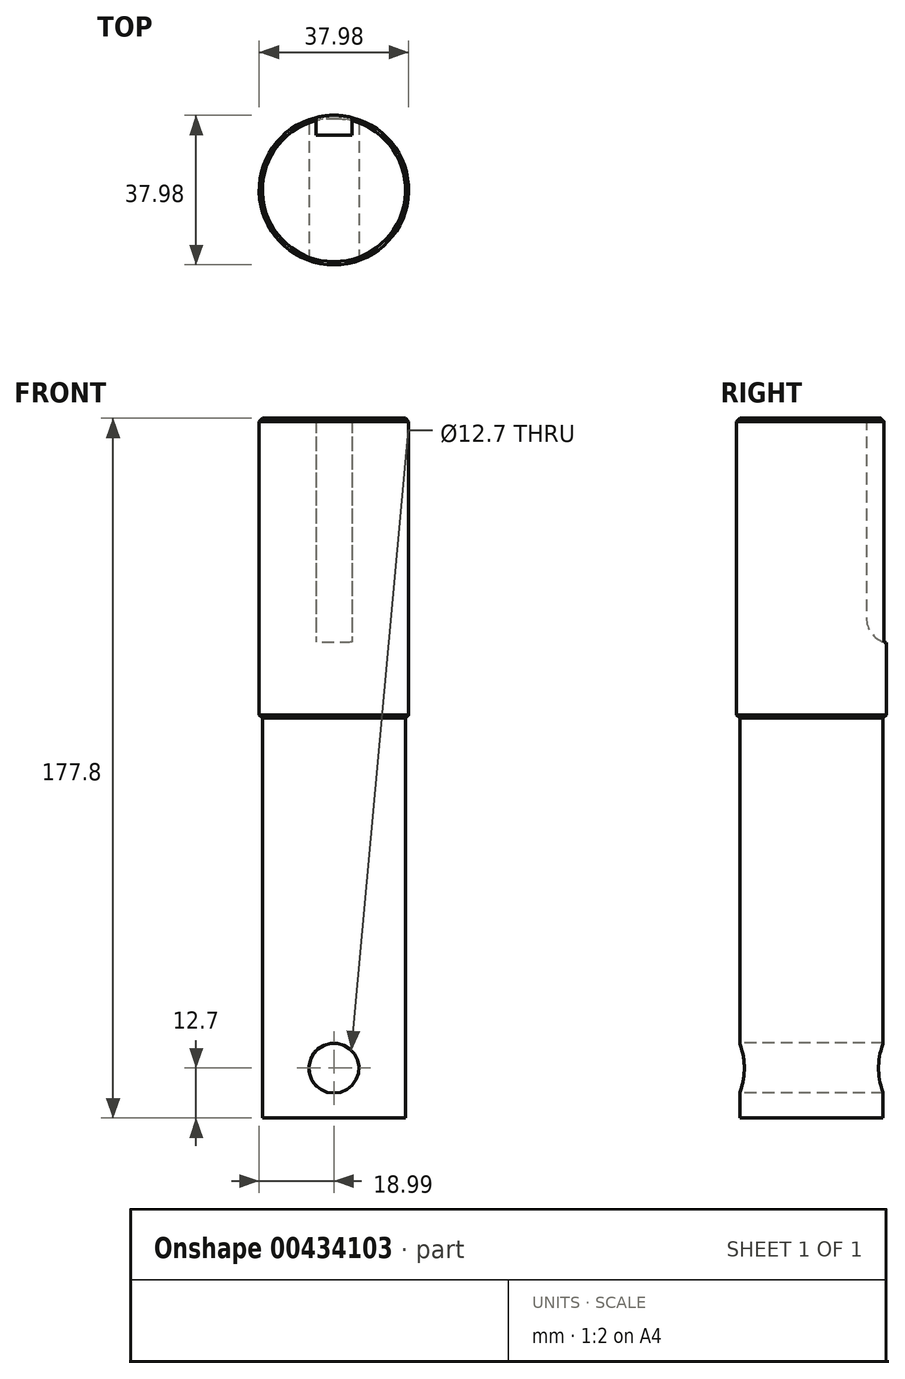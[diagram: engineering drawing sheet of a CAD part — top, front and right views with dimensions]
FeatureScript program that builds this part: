
annotation { "Feature Type Name" : "Feature", "Feature Type Description" : "" }
export const myFeature = defineFeature(function(context is Context, id is Id, definition is map)
    precondition{}
    {
        {
            var Q0;
            Q0=qCreatedBy(makeId("Top.planeOp"),FACE);
            var sketch = newSketch(context, id + "F0", { "sketchPlane" : qUnion([Q0])});
            skCircle(sketch, "E0", {"center": v(0, 0) * mm, "radius": 18.99 * mm});
            skSolve(sketch);
        }
        {
            var Q0;
            Q0=makeQuery(id+"F0.imprint","IMPRINT",FACE,{"disambiguationData":[TD([[makeQuery(id+"F0.imprint","IMPRINT",EDGE,{"derivedFrom":sQuery(id+"F0.wireOp",EDGE,"E0")}),1.0]])]});
            extrude(context, id + "F1", {"entities" : qUnion([Q0]), "endBound" : BoundingType.SYMMETRIC, "depth" : 76.2 * mm});
        }
        {
            var Q0;
            Q0=makeQuery(id+"F1.opExtrude","CAP_EDGE",EDGE,{"disambiguationData":[OSD([sQuery(id+"F0.wireOp",EDGE,"E0")])],"isStart":false});
            var Q1;
            Q1=makeQuery(id+"F1.opExtrude","CAP_EDGE",EDGE,{"disambiguationData":[OSD([sQuery(id+"F0.wireOp",EDGE,"E0")])],"isStart":true});
            chamfer(context, id + "F2", {"entities" : qUnion([Q0, Q1]), "width" : 0.8 * mm, "tangentPropagation" : true});
        }
        {
            var Q0;
            Q0=qCreatedBy(makeId("Right.planeOp"),FACE);
            var sketch = newSketch(context, id + "F3", { "sketchPlane" : qUnion([Q0])});
            skLineSegment(sketch, "E1", {"start": v(13.97, 38.1) * mm, "end": v(13.97, -12.7) * mm});
            skArc(sketch, "E2", {"start": v(13.97, -12.7) * mm, "mid": v(15.4, -16.72) * mm, "end": v(19.05, -18.92) * mm});
            skLineSegment(sketch, "E3", {"start": v(13.97, 38.1) * mm, "end": v(19.05, 38.1) * mm});
            skLineSegment(sketch, "E4", {"start": v(19.05, 38.1) * mm, "end": v(19.05, -18.92) * mm});
            skSolve(sketch);
        }
        {
            var Q0;
            Q0 = qSketchRegion(id + "F3", true);
            extrude(context, id + "F4", {"entities" : qUnion([Q0]), "operationType" : NewBodyOperationType.REMOVE, "endBound" : BoundingType.SYMMETRIC, "depth" : 9.14 * mm});
        }
        {
            var Q0;
            Q0=makeQuery(id+"F1.opExtrude","CAP_FACE",FACE,{"disambiguationData":[OSD([sQuery(id+"F0.wireOp",EDGE,"E0")])],"isStart":true});
            var sketch = newSketch(context, id + "F5", { "sketchPlane" : qUnion([Q0])});
            skSolve(sketch);
        }
        {
            var Q0;
            {var subQ0=sQuery(id+"F0.wireOp",EDGE,"E0");Q0=makeQuery(id+"F5.imprint","IMPRINT",FACE,{"disambiguationData":[TD([[makeQuery(id+"F5.imprint","IMPRINT",EDGE,{"derivedFrom":makeQuery(id+"F2.opChamfer","BLEND_EDGE",EDGE,{"blendedFrom":[makeQuery(id+"F1.opExtrude","CAP_EDGE",EDGE,{"disambiguationData":[OSD([subQ0])],"isStart":true}),makeQuery(id+"F1.opExtrude","CAP_FACE",FACE,{"disambiguationData":[OSD([subQ0])],"isStart":true})],"blendedInto":[makeQuery(id+"F1.opExtrude","CAP_FACE",FACE,{"disambiguationData":[OSD([subQ0])],"isStart":true})]})}),1.0]])]});}
            extrude(context, id + "F6", {"entities" : qUnion([Q0]), "operationType" : NewBodyOperationType.ADD, "depth" : 101.6 * mm});
        }
        {
            var Q0;
            Q0=qCreatedBy(makeId("Front.planeOp"),FACE);
            var sketch = newSketch(context, id + "F7", { "sketchPlane" : qUnion([Q0])});
            skCircle(sketch, "E5", {"center": v(0, -127) * mm, "radius": 6.35 * mm});
            skSolve(sketch);
        }
        {
            var Q0;
            Q0 = qSketchRegion(id + "F7", true);
            extrude(context, id + "F8", {"entities" : qUnion([Q0]), "operationType" : NewBodyOperationType.REMOVE, "endBound" : BoundingType.SYMMETRIC, "oppositeDirection" : true, "depth" : 76.2 * mm});
        }
    });
